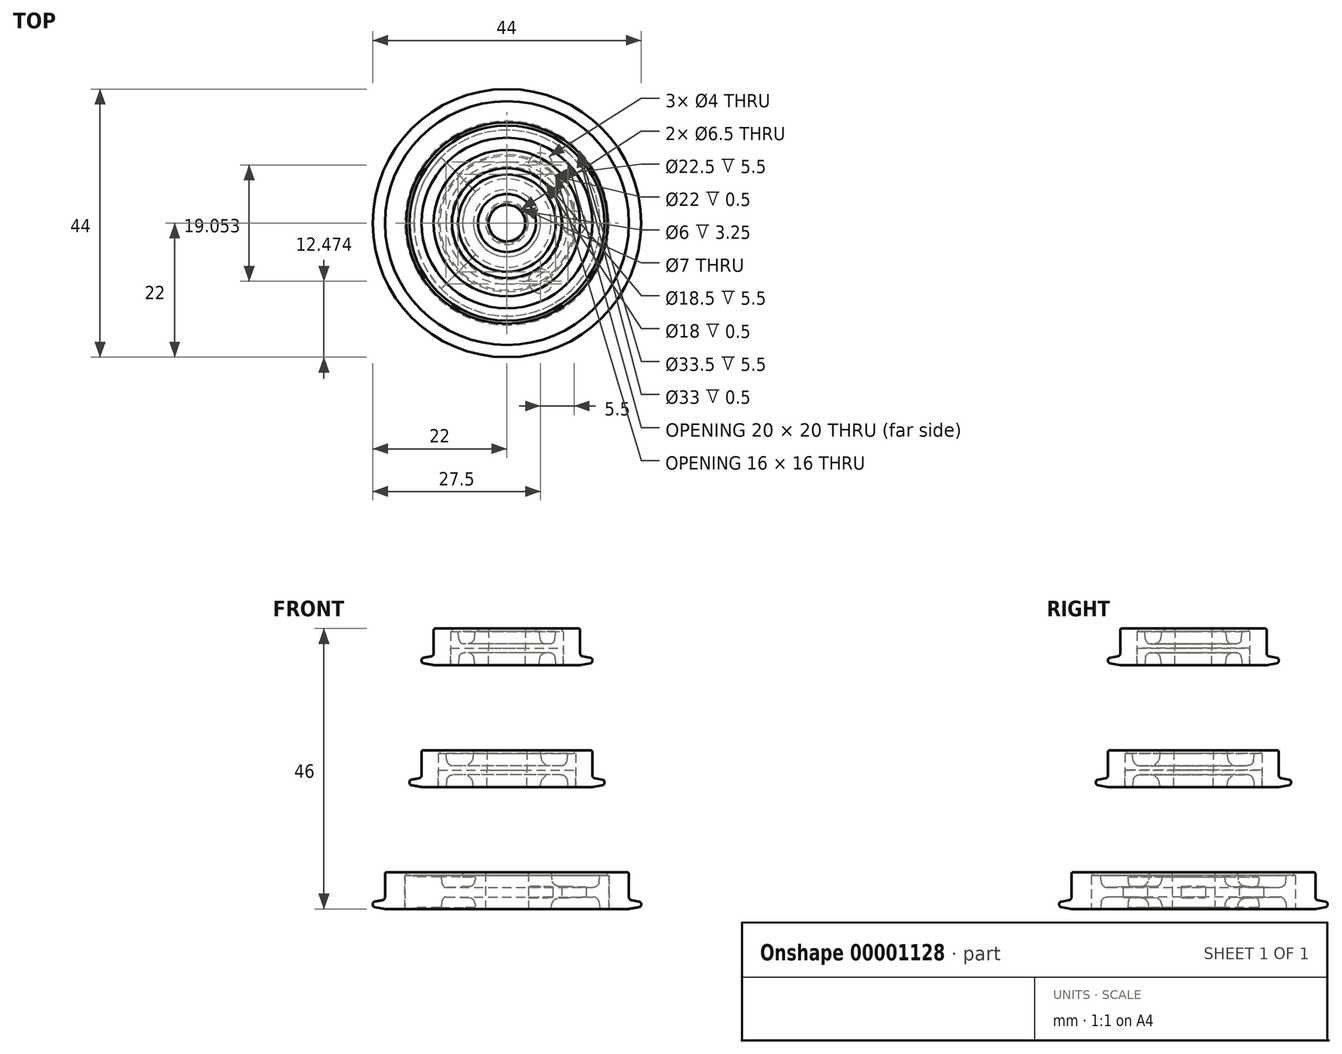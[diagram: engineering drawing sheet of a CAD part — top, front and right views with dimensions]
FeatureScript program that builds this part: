
annotation { "Feature Type Name" : "Feature", "Feature Type Description" : "" }
export const myFeature = defineFeature(function(context is Context, id is Id, definition is map)
    precondition{}
    {
        {
            var Q0;
            Q0=qCreatedBy(makeId("Front.planeOp"),FACE);
            var sketch = newSketch(context, id + "F0", { "sketchPlane" : qUnion([Q0])});
            skLineSegment(sketch, "E0", {"start": v(0, 0) * mm, "end": v(16.75, 0) * mm, "construction": true});
            skPoint(sketch, "E1", {"position": v(3.5, 0) * mm});
            skLineSegment(sketch, "E2", {"start": v(3.5, 0) * mm, "end": v(3.5, 2.75) * mm});
            skLineSegment(sketch, "E3", {"start": v(3.5, 2.75) * mm, "end": v(7.25, 2.75) * mm});
            skLineSegment(sketch, "E4", {"start": v(7.25, 2.75) * mm, "end": v(7.5, 1) * mm});
            skLineSegment(sketch, "E5", {"start": v(7.5, 1) * mm, "end": v(15, 0.75) * mm});
            skLineSegment(sketch, "E6", {"start": v(15, 0.75) * mm, "end": v(15.25, 2.75) * mm});
            skLineSegment(sketch, "E7", {"start": v(15.25, 2.75) * mm, "end": v(16.75, 2.75) * mm});
            skLineSegment(sketch, "E8", {"start": v(16.75, 2.75) * mm, "end": v(16.75, 0) * mm});
            skLineSegment(sketch, "E9", {"start": v(3.5, 0) * mm, "end": v(16.75, 0) * mm});
            skLineSegment(sketch, "E10", {"start": v(0, 0) * mm, "end": v(0, 11.83) * mm, "construction": true});
            skSolve(sketch);
        }
        {
            var Q0;
            Q0=makeQuery(id+"F0.imprint","IMPRINT",FACE,{"disambiguationData":[TD([[makeQuery(id+"F0.imprint","IMPRINT",EDGE,{"derivedFrom":sQuery(id+"F0.wireOp",EDGE,"E2")}),-1.0]])]});
            var Q1;
            Q1=sQuery(id+"F0.wireOp",EDGE,"E10");
            revolve(context, id + "F1", {"entities" : qUnion([Q0]), "axis" : qUnion([Q1]), "revolveType" : RevolveType.FULL});
        }
        {
            var Q0;
            Q0=makeQuery(id+"F1.opRevolve","SWEPT_EDGE",EDGE,{"disambiguationData":[OSD([sQuery(id+"F0.wireOp",EDGE,"E4"),sQuery(id+"F0.wireOp",EDGE,"E5")])]});
            fillet(context, id + "F2", {"entities" : qUnion([Q0]), "radius" : 1.25 * mm, "tangentPropagation" : true, "allowEdgeOverflow" : false});
        }
        {
            var Q0;
            Q0=makeQuery(id+"F1.opRevolve","SWEPT_EDGE",EDGE,{"disambiguationData":[OSD([sQuery(id+"F0.wireOp",EDGE,"E5"),sQuery(id+"F0.wireOp",EDGE,"E6")])]});
            fillet(context, id + "F3", {"entities" : qUnion([Q0]), "radius" : 1 * mm, "tangentPropagation" : true, "allowEdgeOverflow" : false});
        }
        {
            var Q0;
            Q0=makeQuery(id+"F1.opRevolve","SWEPT_BODY",BODY,{"disambiguationData":[OSD([sQuery(id+"F0.wireOp",EDGE,"E2"),sQuery(id+"F0.wireOp",EDGE,"E3"),sQuery(id+"F0.wireOp",EDGE,"E4"),sQuery(id+"F0.wireOp",EDGE,"E5"),sQuery(id+"F0.wireOp",EDGE,"E6"),sQuery(id+"F0.wireOp",EDGE,"E7"),sQuery(id+"F0.wireOp",EDGE,"E8"),sQuery(id+"F0.wireOp",EDGE,"E9")])]});
            var Q1;
            Q1=qCreatedBy(makeId("Top.planeOp"),FACE);
            mirror(context, id + "F4", {"entities" : qUnion([Q0]), "mirrorPlane" : qUnion([Q1])});
        }
        {
            var Q0;
            Q0=makeQuery(id+"F1.opRevolve","SWEPT_FACE",FACE,{"disambiguationData":[OSD([sQuery(id+"F0.wireOp",EDGE,"E3")])]});
            extrude(context, id + "F5", {"entities" : qUnion([Q0]), "operationType" : NewBodyOperationType.ADD, "depth" : 0.5 * mm});
        }
        {
            var Q0;
            Q0=qCreatedBy(makeId("Front.planeOp"),FACE);
            var sketch = newSketch(context, id + "F6", { "sketchPlane" : qUnion([Q0])});
            skLineSegment(sketch, "E11", {"start": v(0, 0) * mm, "end": v(-16.75, 0) * mm, "construction": true});
            skLineSegment(sketch, "E12", {"start": v(-16.75, 0) * mm, "end": v(-16.75, -2.75) * mm});
            skLineSegment(sketch, "E13", {"start": v(-16.75, -2.75) * mm, "end": v(-20, -2.75) * mm});
            skLineSegment(sketch, "E14", {"start": v(-20, -2.75) * mm, "end": v(-22, -2.4) * mm});
            skLineSegment(sketch, "E15", {"start": v(-22, -2.4) * mm, "end": v(-22, -1.6) * mm});
            skLineSegment(sketch, "E16", {"start": v(-22, -1.6) * mm, "end": v(-20, -1.25) * mm});
            skLineSegment(sketch, "E17", {"start": v(-20, -1.25) * mm, "end": v(-20, 3.25) * mm});
            skLineSegment(sketch, "E18", {"start": v(-20, 3.25) * mm, "end": v(-16.5, 3.25) * mm});
            skLineSegment(sketch, "E19", {"start": v(-16.5, 3.25) * mm, "end": v(-16.5, 2.75) * mm});
            skLineSegment(sketch, "E20", {"start": v(-16.5, 2.75) * mm, "end": v(-16.75, 2.75) * mm});
            skLineSegment(sketch, "E21", {"start": v(-16.75, 2.75) * mm, "end": v(-16.75, 0) * mm});
            skLineSegment(sketch, "E22", {"start": v(0, 9.74) * mm, "end": v(0, 0) * mm, "construction": true});
            skSolve(sketch);
        }
        {
            var Q0;
            Q0=makeQuery(id+"F6.imprint","IMPRINT",FACE,{"disambiguationData":[TD([[makeQuery(id+"F6.imprint","IMPRINT",EDGE,{"derivedFrom":sQuery(id+"F6.wireOp",EDGE,"E12")}),-1.0]])]});
            var Q1;
            Q1=sQuery(id+"F6.wireOp",EDGE,"E22");
            revolve(context, id + "F7", {"entities" : qUnion([Q0]), "axis" : qUnion([Q1]), "revolveType" : RevolveType.FULL});
        }
        {
            var Q0;
            Q0=makeQuery(id+"F7.opRevolve","SWEPT_EDGE",EDGE,{"disambiguationData":[OSD([sQuery(id+"F6.wireOp",EDGE,"E16"),sQuery(id+"F6.wireOp",EDGE,"E17")])]});
            fillet(context, id + "F8", {"entities" : qUnion([Q0]), "radius" : 0.5 * mm, "tangentPropagation" : true, "allowEdgeOverflow" : false});
        }
        {
            var Q0;
            Q0=makeQuery(id+"F7.opRevolve","SWEPT_EDGE",EDGE,{"disambiguationData":[OSD([sQuery(id+"F6.wireOp",EDGE,"E15"),sQuery(id+"F6.wireOp",EDGE,"E16")])]});
            var Q1;
            Q1=makeQuery(id+"F7.opRevolve","SWEPT_FACE",FACE,{"disambiguationData":[OSD([sQuery(id+"F6.wireOp",EDGE,"E15")])]});
            fillet(context, id + "F9", {"entities" : qUnion([Q0, Q1]), "radius" : 0.4 * mm, "tangentPropagation" : true, "allowEdgeOverflow" : false});
        }
        {
            var Q0;
            Q0=qCreatedBy(makeId("Front.planeOp"),FACE);
            var sketch = newSketch(context, id + "F10", { "sketchPlane" : qUnion([Q0])});
            skLineSegment(sketch, "E23", {"start": v(0, 0) * mm, "end": v(-24.96, 0) * mm, "construction": true});
            skLineSegment(sketch, "E24", {"start": v(0, 0) * mm, "end": v(0, 16.16) * mm, "construction": true});
            skLineSegment(sketch, "E25", {"start": v(-7.25, 0) * mm, "end": v(-7.25, 2.5) * mm});
            skLineSegment(sketch, "E26", {"start": v(-7.25, 2.5) * mm, "end": v(-15.25, 2.5) * mm});
            skLineSegment(sketch, "E27", {"start": v(-15.25, 2.5) * mm, "end": v(-15.25, -2.5) * mm});
            skLineSegment(sketch, "E28", {"start": v(-15.25, -2.5) * mm, "end": v(-7.25, -2.5) * mm});
            skLineSegment(sketch, "E29", {"start": v(-7.25, -2.5) * mm, "end": v(-7.25, 0) * mm});
            skSolve(sketch);
        }
        {
            var Q0;
            Q0=makeQuery(id+"F10.imprint","IMPRINT",FACE,{"disambiguationData":[TD([[makeQuery(id+"F10.imprint","IMPRINT",EDGE,{"derivedFrom":sQuery(id+"F10.wireOp",EDGE,"E26")}),1.0]])]});
            var Q1;
            Q1=sQuery(id+"F10.wireOp",EDGE,"E24");
            revolve(context, id + "F11", {"operationType" : NewBodyOperationType.ADD, "entities" : qUnion([Q0]), "axis" : qUnion([Q1]), "revolveType" : RevolveType.TWO_DIRECTIONS, "angle" : 45 * degree, "angleBack" : 315 * degree});
        }
        {
            var Q0;
            Q0=qCreatedBy(makeId("Top.planeOp"),FACE);
            var sketch = newSketch(context, id + "F12", { "sketchPlane" : qUnion([Q0])});
            skLineSegment(sketch, "E30", {"start": v(0, 0) * mm, "end": v(5.5, -9.53) * mm, "construction": true});
            skCircle(sketch, "E31", {"center": v(5.5, -9.53) * mm, "radius": 2 * mm});
            skLineSegment(sketch, "E32", {"start": v(0, 0) * mm, "end": v(-8.82, 0) * mm, "construction": true});
            skSolve(sketch);
        }
        {
            var Q0;
            Q0=makeQuery(id+"F12.imprint","IMPRINT",FACE,{"disambiguationData":[TD([[makeQuery(id+"F12.imprint","IMPRINT",EDGE,{"derivedFrom":sQuery(id+"F12.wireOp",EDGE,"E31")}),1.0]])]});
            extrude(context, id + "F13", {"entities" : qUnion([Q0]), "endBound" : BoundingType.SYMMETRIC, "depth" : 10 * mm});
        }
        {
            var Q0;
            Q0=qCreatedBy(makeId("Front.planeOp"),FACE);
            var sketch = newSketch(context, id + "F14", { "sketchPlane" : qUnion([Q0])});
            skLineSegment(sketch, "E33", {"start": v(0, 0) * mm, "end": v(0, 19.31) * mm, "construction": true});
            skSolve(sketch);
        }
        {
            var Q0;
            Q0=makeQuery(id+"F13.opExtrude","SWEPT_BODY",BODY,{"disambiguationData":[OSD([sQuery(id+"F12.wireOp",EDGE,"E31")])]});
            var Q1;
            Q1=sQuery(id+"F14.wireOp",EDGE,"E33");
            circularPattern(context, id + "F15", {"entities" : qUnion([Q0]), "axis" : qUnion([Q1]), "angle" : 60 * degree, "instanceCount" : 3});
        }
        {
            var Q0;
            Q0=makeQuery(id+"F13.opExtrude","SWEPT_BODY",BODY,{"disambiguationData":[OSD([sQuery(id+"F12.wireOp",EDGE,"E31")])]});
            var Q1;
            Q1=makeQuery(id+"F15.opPattern","COPY",BODY,{"derivedFrom":makeQuery(id+"F13.opExtrude","SWEPT_BODY",BODY,{"disambiguationData":[OSD([sQuery(id+"F12.wireOp",EDGE,"E31")])]}),"instanceName":"1"});
            var Q2;
            Q2=makeQuery(id+"F15.opPattern","COPY",BODY,{"derivedFrom":makeQuery(id+"F13.opExtrude","SWEPT_BODY",BODY,{"disambiguationData":[OSD([sQuery(id+"F12.wireOp",EDGE,"E31")])]}),"instanceName":"2"});
            var Q3;
            Q3=makeQuery(id+"F1.opRevolve","SWEPT_BODY",BODY,{"disambiguationData":[OSD([sQuery(id+"F0.wireOp",EDGE,"E2"),sQuery(id+"F0.wireOp",EDGE,"E3"),sQuery(id+"F0.wireOp",EDGE,"E4"),sQuery(id+"F0.wireOp",EDGE,"E5"),sQuery(id+"F0.wireOp",EDGE,"E6"),sQuery(id+"F0.wireOp",EDGE,"E7"),sQuery(id+"F0.wireOp",EDGE,"E8"),sQuery(id+"F0.wireOp",EDGE,"E9")])]});
            booleanBodies(context, id + "F16", {"operationType" : BooleanOperationType.SUBTRACTION, "tools" : qUnion([Q0, Q1, Q2]), "targets" : qUnion([Q3])});
        }
        {
            var Q0;
            Q0=makeQuery(id+"F5.opExtrude","CAP_EDGE",EDGE,{"disambiguationData":[OSD([sQuery(id+"F0.wireOp",EDGE,"E3"),sQuery(id+"F0.wireOp",EDGE,"E4")])],"isStart":false});
            var Q1;
            Q1=makeQuery(id+"F11.opRevolve","CAP_EDGE",EDGE,{"disambiguationData":[OSD([sQuery(id+"F10.wireOp",EDGE,"E26")])],"isStart":false});
            var Q2;
            Q2=makeQuery(id+"F11.opRevolve","CAP_EDGE",EDGE,{"disambiguationData":[OSD([sQuery(id+"F10.wireOp",EDGE,"E28")])],"isStart":true});
            var Q3;
            Q3=makeQuery(id+"F7.opRevolve","SWEPT_EDGE",EDGE,{"disambiguationData":[OSD([sQuery(id+"F6.wireOp",EDGE,"E17"),sQuery(id+"F6.wireOp",EDGE,"E18")])]});
            var Q4;
            Q4=makeQuery(id+"F11.opRevolve","CAP_EDGE",EDGE,{"disambiguationData":[OSD([sQuery(id+"F10.wireOp",EDGE,"E26")])],"isStart":true});
            var Q5;
            Q5=makeQuery(id+"F11.opRevolve","CAP_EDGE",EDGE,{"disambiguationData":[OSD([sQuery(id+"F10.wireOp",EDGE,"E28")])],"isStart":false});
            var Q6;
            {var subQ0=sQuery(id+"F0.wireOp",EDGE,"E5");Q6=makeQuery(id+"F4.opPattern","COPY",EDGE,{"derivedFrom":makeQuery(id+"F3.opFillet","BLEND_EDGE",EDGE,{"blendedFrom":[makeQuery(id+"F1.opRevolve","SWEPT_EDGE",EDGE,{"disambiguationData":[OSD([subQ0,sQuery(id+"F0.wireOp",EDGE,"E6")])]}),makeQuery(id+"F1.opRevolve","SWEPT_FACE",FACE,{"disambiguationData":[OSD([subQ0])]})],"blendedInto":[makeQuery(id+"F1.opRevolve","SWEPT_FACE",FACE,{"disambiguationData":[OSD([subQ0])]})]}),"instanceName":"1"});}
            var Q7;
            Q7=makeQuery(id+"F4.opPattern","COPY",EDGE,{"derivedFrom":makeQuery(id+"F1.opRevolve","SWEPT_EDGE",EDGE,{"disambiguationData":[OSD([sQuery(id+"F0.wireOp",EDGE,"E3"),sQuery(id+"F0.wireOp",EDGE,"E4")])]}),"instanceName":"1"});
            fillet(context, id + "F17", {"entities" : qUnion([Q0, Q1, Q2, Q3, Q4, Q5, Q6, Q7]), "radius" : 0.25 * mm, "tangentPropagation" : true, "allowEdgeOverflow" : false});
        }
        {
            var Q0;
            Q0=qCreatedBy(makeId("Front.planeOp"),FACE);
            var sketch = newSketch(context, id + "F18", { "sketchPlane" : qUnion([Q0])});
            skLineSegment(sketch, "E34", {"start": v(0, 20) * mm, "end": v(-3.25, 20) * mm, "construction": true});
            skLineSegment(sketch, "E35", {"start": v(0, 19.54) * mm, "end": v(0, 20) * mm, "construction": true});
            skLineSegment(sketch, "E36", {"start": v(-3.25, 20) * mm, "end": v(-11.25, 20) * mm});
            skLineSegment(sketch, "E37", {"start": v(-11.25, 20) * mm, "end": v(-11.25, 22.75) * mm});
            skLineSegment(sketch, "E38", {"start": v(-11.25, 22.75) * mm, "end": v(-10, 22.75) * mm});
            skLineSegment(sketch, "E39", {"start": v(-10, 22.75) * mm, "end": v(-9.75, 20.75) * mm});
            skLineSegment(sketch, "E40", {"start": v(-9.75, 20.75) * mm, "end": v(-5.75, 20.75) * mm});
            skLineSegment(sketch, "E41", {"start": v(-5.75, 20.75) * mm, "end": v(-5.5, 22.75) * mm});
            skLineSegment(sketch, "E42", {"start": v(-5.5, 22.75) * mm, "end": v(-3.25, 22.75) * mm});
            skLineSegment(sketch, "E43", {"start": v(-3.25, 22.75) * mm, "end": v(-3.25, 20) * mm});
            skLineSegment(sketch, "E44", {"start": v(0, 0) * mm, "end": v(0, 20) * mm, "construction": true});
            skSolve(sketch);
        }
        {
            var Q0;
            Q0=makeQuery(id+"F18.imprint","IMPRINT",FACE,{"disambiguationData":[TD([[makeQuery(id+"F18.imprint","IMPRINT",EDGE,{"derivedFrom":sQuery(id+"F18.wireOp",EDGE,"E36")}),-1.0]])]});
            var Q1;
            Q1=sQuery(id+"F18.wireOp",EDGE,"E35");
            revolve(context, id + "F19", {"entities" : qUnion([Q0]), "axis" : qUnion([Q1]), "revolveType" : RevolveType.FULL});
        }
        {
            var Q0;
            Q0=makeQuery(id+"F19.opRevolve","SWEPT_EDGE",EDGE,{"disambiguationData":[OSD([sQuery(id+"F18.wireOp",EDGE,"E40"),sQuery(id+"F18.wireOp",EDGE,"E41")])]});
            fillet(context, id + "F20", {"entities" : qUnion([Q0]), "radius" : 1.5 * mm, "tangentPropagation" : true, "allowEdgeOverflow" : false});
        }
        {
            var Q0;
            Q0=makeQuery(id+"F19.opRevolve","SWEPT_EDGE",EDGE,{"disambiguationData":[OSD([sQuery(id+"F18.wireOp",EDGE,"E39"),sQuery(id+"F18.wireOp",EDGE,"E40")])]});
            fillet(context, id + "F21", {"entities" : qUnion([Q0]), "radius" : 1 * mm, "tangentPropagation" : true, "allowEdgeOverflow" : false});
        }
        {
            var Q0;
            Q0=makeQuery(id+"F19.opRevolve","SWEPT_BODY",BODY,{"disambiguationData":[OSD([sQuery(id+"F18.wireOp",EDGE,"E36"),sQuery(id+"F18.wireOp",EDGE,"E37"),sQuery(id+"F18.wireOp",EDGE,"E38"),sQuery(id+"F18.wireOp",EDGE,"E39"),sQuery(id+"F18.wireOp",EDGE,"E40"),sQuery(id+"F18.wireOp",EDGE,"E41"),sQuery(id+"F18.wireOp",EDGE,"E42"),sQuery(id+"F18.wireOp",EDGE,"E43")])]});
            var Q1;
            Q1=makeQuery(id+"F19.opRevolve","SWEPT_FACE",FACE,{"disambiguationData":[OSD([sQuery(id+"F18.wireOp",EDGE,"E36")])]});
            mirror(context, id + "F22", {"entities" : qUnion([Q0]), "mirrorPlane" : qUnion([Q1])});
        }
        {
            var Q0;
            Q0=makeQuery(id+"F19.opRevolve","SWEPT_FACE",FACE,{"disambiguationData":[OSD([sQuery(id+"F18.wireOp",EDGE,"E42")])]});
            extrude(context, id + "F23", {"entities" : qUnion([Q0]), "operationType" : NewBodyOperationType.ADD, "depth" : 0.5 * mm});
        }
        {
            var Q0;
            Q0=qCreatedBy(makeId("Front.planeOp"),FACE);
            var sketch = newSketch(context, id + "F24", { "sketchPlane" : qUnion([Q0])});
            skLineSegment(sketch, "E45", {"start": v(0, 0) * mm, "end": v(0, 40) * mm, "construction": true});
            skLineSegment(sketch, "E46", {"start": v(0, 20) * mm, "end": v(-11.25, 20) * mm, "construction": true});
            skLineSegment(sketch, "E47", {"start": v(-11.25, 20) * mm, "end": v(-11.25, 17.25) * mm});
            skLineSegment(sketch, "E48", {"start": v(-11.25, 17.25) * mm, "end": v(-14, 17.25) * mm});
            skLineSegment(sketch, "E49", {"start": v(-11.25, 20) * mm, "end": v(-11.25, 22.75) * mm});
            skLineSegment(sketch, "E50", {"start": v(-11.25, 22.75) * mm, "end": v(-11, 22.75) * mm});
            skLineSegment(sketch, "E51", {"start": v(-11, 22.75) * mm, "end": v(-11, 23.25) * mm});
            skLineSegment(sketch, "E52", {"start": v(-11, 23.25) * mm, "end": v(-14, 23.25) * mm});
            skLineSegment(sketch, "E53", {"start": v(-14, 23.25) * mm, "end": v(-14, 18.75) * mm});
            skLineSegment(sketch, "E54", {"start": v(-14, 18.75) * mm, "end": v(-16, 18.4) * mm});
            skLineSegment(sketch, "E55", {"start": v(-14, 17.25) * mm, "end": v(-16, 17.6) * mm});
            skLineSegment(sketch, "E56", {"start": v(-16, 17.6) * mm, "end": v(-16, 18.4) * mm});
            skSolve(sketch);
        }
        {
            var Q0;
            Q0=makeQuery(id+"F24.imprint","IMPRINT",FACE,{"disambiguationData":[TD([[makeQuery(id+"F24.imprint","IMPRINT",EDGE,{"derivedFrom":sQuery(id+"F24.wireOp",EDGE,"E47")}),-1.0]])]});
            var Q1;
            Q1=sQuery(id+"F24.wireOp",EDGE,"E45");
            revolve(context, id + "F25", {"entities" : qUnion([Q0]), "axis" : qUnion([Q1]), "revolveType" : RevolveType.FULL});
        }
        {
            var Q0;
            Q0=makeQuery(id+"F25.opRevolve","SWEPT_EDGE",EDGE,{"disambiguationData":[OSD([sQuery(id+"F24.wireOp",EDGE,"E53"),sQuery(id+"F24.wireOp",EDGE,"E54")])]});
            fillet(context, id + "F26", {"entities" : qUnion([Q0]), "radius" : 0.5 * mm, "tangentPropagation" : true, "allowEdgeOverflow" : false});
        }
        {
            var Q0;
            Q0=makeQuery(id+"F25.opRevolve","SWEPT_EDGE",EDGE,{"disambiguationData":[OSD([sQuery(id+"F24.wireOp",EDGE,"E55"),sQuery(id+"F24.wireOp",EDGE,"E56")])]});
            var Q1;
            Q1=makeQuery(id+"F25.opRevolve","SWEPT_EDGE",EDGE,{"disambiguationData":[OSD([sQuery(id+"F24.wireOp",EDGE,"E54"),sQuery(id+"F24.wireOp",EDGE,"E56")])]});
            fillet(context, id + "F27", {"entities" : qUnion([Q0, Q1]), "radius" : 0.4 * mm, "tangentPropagation" : true, "allowEdgeOverflow" : false});
        }
        {
            var Q0;
            Q0=makeQuery(id+"F23.opExtrude","CAP_EDGE",EDGE,{"disambiguationData":[OSD([sQuery(id+"F18.wireOp",EDGE,"E41"),sQuery(id+"F18.wireOp",EDGE,"E42")])],"isStart":false});
            var Q1;
            Q1=makeQuery(id+"F22.opPattern","COPY",EDGE,{"derivedFrom":makeQuery(id+"F19.opRevolve","SWEPT_EDGE",EDGE,{"disambiguationData":[OSD([sQuery(id+"F18.wireOp",EDGE,"E41"),sQuery(id+"F18.wireOp",EDGE,"E42")])]}),"instanceName":"1"});
            var Q2;
            Q2=makeQuery(id+"F25.opRevolve","SWEPT_EDGE",EDGE,{"disambiguationData":[OSD([sQuery(id+"F24.wireOp",EDGE,"E52"),sQuery(id+"F24.wireOp",EDGE,"E53")])]});
            fillet(context, id + "F28", {"entities" : qUnion([Q0, Q1, Q2]), "radius" : 0.25 * mm, "tangentPropagation" : true, "allowEdgeOverflow" : false});
        }
        {
            var Q0;
            Q0=makeQuery(id+"F23.opExtrude","CAP_FACE",FACE,{"disambiguationData":[OSD([sQuery(id+"F18.wireOp",EDGE,"E42")])],"isStart":false});
            var sketch = newSketch(context, id + "F29", { "sketchPlane" : qUnion([Q0])});
            skLineSegment(sketch, "E57", {"start": v(0, 0) * mm, "end": v(2.75, -4.76) * mm, "construction": true});
            skCircle(sketch, "E58", {"center": v(2.75, -4.76) * mm, "radius": 1.25 * mm});
            skLineSegment(sketch, "E59", {"start": v(0, 0) * mm, "end": v(7.85, 0) * mm, "construction": true});
            skSolve(sketch);
        }
        {
            var Q0;
            Q0=qCreatedBy(makeId("Front.planeOp"),FACE);
            var sketch = newSketch(context, id + "F30", { "sketchPlane" : qUnion([Q0])});
            skLineSegment(sketch, "E60", {"start": v(0, 0) * mm, "end": v(0, 38) * mm, "construction": true});
            skSolve(sketch);
        }
        {
            var Q0;
            Q0=qCreatedBy(makeId("Front.planeOp"),FACE);
            var sketch = newSketch(context, id + "F31", { "sketchPlane" : qUnion([Q0])});
            skLineSegment(sketch, "E61", {"start": v(0, 0) * mm, "end": v(0, 40) * mm, "construction": true});
            skLineSegment(sketch, "E62", {"start": v(0, 40) * mm, "end": v(-3, 40) * mm, "construction": true});
            skLineSegment(sketch, "E63", {"start": v(-3, 40) * mm, "end": v(-9.25, 40) * mm});
            skLineSegment(sketch, "E64", {"start": v(-9.25, 40) * mm, "end": v(-9.25, 42.75) * mm});
            skLineSegment(sketch, "E65", {"start": v(-9.25, 42.75) * mm, "end": v(-8, 42.75) * mm});
            skLineSegment(sketch, "E66", {"start": v(-8, 42.75) * mm, "end": v(-7.75, 40.75) * mm});
            skLineSegment(sketch, "E67", {"start": v(-7.75, 40.75) * mm, "end": v(-5.5, 40.75) * mm});
            skLineSegment(sketch, "E68", {"start": v(-5.5, 40.75) * mm, "end": v(-5.25, 42.75) * mm});
            skLineSegment(sketch, "E69", {"start": v(-5.25, 42.75) * mm, "end": v(-3, 42.75) * mm});
            skLineSegment(sketch, "E70", {"start": v(-3, 42.75) * mm, "end": v(-3, 40) * mm});
            skSolve(sketch);
        }
        {
            var Q0;
            Q0=makeQuery(id+"F31.imprint","IMPRINT",FACE,{"disambiguationData":[TD([[makeQuery(id+"F31.imprint","IMPRINT",EDGE,{"derivedFrom":sQuery(id+"F31.wireOp",EDGE,"E63")}),-1.0]])]});
            var Q1;
            Q1=sQuery(id+"F31.wireOp",EDGE,"E61");
            revolve(context, id + "F32", {"entities" : qUnion([Q0]), "axis" : qUnion([Q1]), "revolveType" : RevolveType.FULL});
        }
        {
            var Q0;
            Q0=makeQuery(id+"F32.opRevolve","SWEPT_EDGE",EDGE,{"disambiguationData":[OSD([sQuery(id+"F31.wireOp",EDGE,"E67"),sQuery(id+"F31.wireOp",EDGE,"E68")])]});
            fillet(context, id + "F33", {"entities" : qUnion([Q0]), "radius" : 1 * mm, "tangentPropagation" : true, "allowEdgeOverflow" : false});
        }
        {
            var Q0;
            Q0=makeQuery(id+"F32.opRevolve","SWEPT_EDGE",EDGE,{"disambiguationData":[OSD([sQuery(id+"F31.wireOp",EDGE,"E66"),sQuery(id+"F31.wireOp",EDGE,"E67")])]});
            fillet(context, id + "F34", {"entities" : qUnion([Q0]), "radius" : 0.75 * mm, "tangentPropagation" : true, "allowEdgeOverflow" : false});
        }
        {
            var Q0;
            Q0=makeQuery(id+"F32.opRevolve","SWEPT_BODY",BODY,{"disambiguationData":[OSD([sQuery(id+"F31.wireOp",EDGE,"E63"),sQuery(id+"F31.wireOp",EDGE,"E64"),sQuery(id+"F31.wireOp",EDGE,"E65"),sQuery(id+"F31.wireOp",EDGE,"E66"),sQuery(id+"F31.wireOp",EDGE,"E67"),sQuery(id+"F31.wireOp",EDGE,"E68"),sQuery(id+"F31.wireOp",EDGE,"E69"),sQuery(id+"F31.wireOp",EDGE,"E70")])]});
            var Q1;
            Q1=makeQuery(id+"F32.opRevolve","SWEPT_FACE",FACE,{"disambiguationData":[OSD([sQuery(id+"F31.wireOp",EDGE,"E63")])]});
            mirror(context, id + "F35", {"entities" : qUnion([Q0]), "mirrorPlane" : qUnion([Q1])});
        }
        {
            var Q0;
            Q0=makeQuery(id+"F32.opRevolve","SWEPT_FACE",FACE,{"disambiguationData":[OSD([sQuery(id+"F31.wireOp",EDGE,"E69")])]});
            var sketch = newSketch(context, id + "F36", { "sketchPlane" : qUnion([Q0])});
            skCircle(sketch, "E71", {"center": v(0, 0) * mm, "radius": 4.75 * mm});
            skSolve(sketch);
        }
        {
            var Q0;
            Q0=makeQuery(id+"F36.imprint","IMPRINT",FACE,{"disambiguationData":[TD([[makeQuery(id+"F36.imprint","IMPRINT",EDGE,{"derivedFrom":sQuery(id+"F36.wireOp",EDGE,"E71")}),1.0]])]});
            extrude(context, id + "F37", {"entities" : qUnion([Q0]), "operationType" : NewBodyOperationType.ADD, "depth" : 0.5 * mm});
        }
        {
            var Q0;
            Q0=qCreatedBy(makeId("Front.planeOp"),FACE);
            var sketch = newSketch(context, id + "F38", { "sketchPlane" : qUnion([Q0])});
            skLineSegment(sketch, "E72", {"start": v(0, 0) * mm, "end": v(0, 40) * mm, "construction": true});
            skLineSegment(sketch, "E73", {"start": v(0, 40) * mm, "end": v(-9.25, 40) * mm, "construction": true});
            skLineSegment(sketch, "E74", {"start": v(-9.25, 40) * mm, "end": v(-9.25, 37.25) * mm});
            skLineSegment(sketch, "E75", {"start": v(-9.25, 37.25) * mm, "end": v(-12, 37.25) * mm});
            skLineSegment(sketch, "E76", {"start": v(-12, 37.25) * mm, "end": v(-14, 37.6) * mm});
            skLineSegment(sketch, "E77", {"start": v(-14, 37.6) * mm, "end": v(-14, 38.4) * mm});
            skLineSegment(sketch, "E78", {"start": v(-14, 38.4) * mm, "end": v(-12, 38.75) * mm});
            skLineSegment(sketch, "E79", {"start": v(-12, 38.75) * mm, "end": v(-12, 43.25) * mm});
            skLineSegment(sketch, "E80", {"start": v(-12, 43.25) * mm, "end": v(-9, 43.25) * mm});
            skLineSegment(sketch, "E81", {"start": v(-9, 43.25) * mm, "end": v(-9, 42.75) * mm});
            skLineSegment(sketch, "E82", {"start": v(-9, 42.75) * mm, "end": v(-9.25, 42.75) * mm});
            skLineSegment(sketch, "E83", {"start": v(-9.25, 42.75) * mm, "end": v(-9.25, 40) * mm});
            skSolve(sketch);
        }
        {
            var Q0;
            Q0=makeQuery(id+"F38.imprint","IMPRINT",FACE,{"disambiguationData":[TD([[makeQuery(id+"F38.imprint","IMPRINT",EDGE,{"derivedFrom":sQuery(id+"F38.wireOp",EDGE,"E74")}),-1.0]])]});
            var Q1;
            Q1=sQuery(id+"F38.wireOp",EDGE,"E72");
            revolve(context, id + "F39", {"entities" : qUnion([Q0]), "axis" : qUnion([Q1]), "revolveType" : RevolveType.FULL});
        }
        {
            var Q0;
            Q0=makeQuery(id+"F39.opRevolve","SWEPT_EDGE",EDGE,{"disambiguationData":[OSD([sQuery(id+"F38.wireOp",EDGE,"E78"),sQuery(id+"F38.wireOp",EDGE,"E79")])]});
            fillet(context, id + "F40", {"entities" : qUnion([Q0]), "radius" : 0.5 * mm, "tangentPropagation" : true, "allowEdgeOverflow" : false});
        }
        {
            var Q0;
            Q0=makeQuery(id+"F32.opRevolve","SWEPT_EDGE",EDGE,{"disambiguationData":[OSD([sQuery(id+"F31.wireOp",EDGE,"E68"),sQuery(id+"F31.wireOp",EDGE,"E69")])]});
            var Q1;
            Q1=makeQuery(id+"F37.opExtrude","CAP_EDGE",EDGE,{"disambiguationData":[OSD([sQuery(id+"F36.wireOp",EDGE,"E71")])],"isStart":false});
            var Q2;
            Q2=makeQuery(id+"F35.opPattern","COPY",EDGE,{"derivedFrom":makeQuery(id+"F32.opRevolve","SWEPT_EDGE",EDGE,{"disambiguationData":[OSD([sQuery(id+"F31.wireOp",EDGE,"E68"),sQuery(id+"F31.wireOp",EDGE,"E69")])]}),"instanceName":"1"});
            var Q3;
            Q3=makeQuery(id+"F39.opRevolve","SWEPT_EDGE",EDGE,{"disambiguationData":[OSD([sQuery(id+"F38.wireOp",EDGE,"E79"),sQuery(id+"F38.wireOp",EDGE,"E80")])]});
            fillet(context, id + "F41", {"entities" : qUnion([Q0, Q1, Q2, Q3]), "radius" : 0.25 * mm, "tangentPropagation" : true, "allowEdgeOverflow" : false});
        }
        {
            var Q0;
            Q0=makeQuery(id+"F39.opRevolve","SWEPT_EDGE",EDGE,{"disambiguationData":[OSD([sQuery(id+"F38.wireOp",EDGE,"E77"),sQuery(id+"F38.wireOp",EDGE,"E78")])]});
            var Q1;
            Q1=makeQuery(id+"F39.opRevolve","SWEPT_EDGE",EDGE,{"disambiguationData":[OSD([sQuery(id+"F38.wireOp",EDGE,"E76"),sQuery(id+"F38.wireOp",EDGE,"E77")])]});
            fillet(context, id + "F42", {"entities" : qUnion([Q0, Q1]), "radius" : 0.4 * mm, "tangentPropagation" : true, "allowEdgeOverflow" : false});
        }
    });
